FCSTD DOCUMENT  (FreeCAD 0.20R)
Label: id5
License: All rights reserved
LicenseURL: http://en.wikipedia.org/wiki/All_rights_reserved
objects: Part::Fillet×17, Part::FeaturePython×8, Sketcher::SketchObject×7, Part::Extrusion×7, Part::Chamfer×4, Drawing::FeatureViewPart×2, Drawing::FeaturePage×1, Part::MultiFuse×1, Part::Box×1, Part::Cut×1
note: 46 computed .brp shape members not serialized (recipe doc carries the construction recipe); baked Part::Feature solids carry a one-line shape summary decoded from their .brp

FEATURE [Sketcher::SketchObject] Sketch  label="Плата"
  FullyConstrained = false
  MapMode = 2
  Placement = pos=(91,0,0) rot=(0,0,1;0rad)
  sketch-geometry (16):
    g0: LineSegment StartX=-40.8321 StartY=93.3922 StartZ=0 EndX=42.1679 EndY=93.3922 EndZ=0
    g1: LineSegment StartX=42.1679 StartY=93.3922 StartZ=0 EndX=42.1679 EndY=15.3922 EndZ=0
    g2: LineSegment StartX=42.1679 StartY=15.3922 StartZ=0 EndX=-40.8321 EndY=15.3922 EndZ=0
    g3: LineSegment StartX=-40.8321 StartY=15.3922 StartZ=0 EndX=-40.8321 EndY=93.3922 EndZ=0
    g4: Circle CenterX=-38.5461 CenterY=91.1067 CenterZ=0 NormalX=0 NormalY=0 NormalZ=1 AngleXU=0 Radius=1.524
    g5: Circle CenterX=39.6579 CenterY=91.1022 CenterZ=0 NormalX=0 NormalY=0 NormalZ=1 AngleXU=0 Radius=1.524
    g6: LineSegment StartX=-38.5461 StartY=91.1067 StartZ=0 EndX=-40.8321 EndY=91.1067 EndZ=0
    g7: LineSegment StartX=-38.5461 StartY=91.1067 StartZ=0 EndX=-38.4965 EndY=93.3922 EndZ=0
    g8: LineSegment StartX=39.6579 StartY=91.1022 StartZ=0 EndX=42.1679 EndY=91.1022 EndZ=0
    g9: LineSegment StartX=39.6579 StartY=91.1022 StartZ=0 EndX=39.6579 EndY=93.3922 EndZ=0
    g10: Circle CenterX=-38.5461 CenterY=17.6782 CenterZ=0 NormalX=0 NormalY=0 NormalZ=1 AngleXU=0 Radius=1.524
    g11: LineSegment StartX=-38.5461 StartY=17.6782 StartZ=0 EndX=-40.8321 EndY=17.6782 EndZ=0
    g12: LineSegment StartX=-38.5461 StartY=17.6782 StartZ=0 EndX=-38.5461 EndY=15.3922 EndZ=0
    g13: Circle CenterX=39.7079 CenterY=17.7672 CenterZ=0 NormalX=0 NormalY=0 NormalZ=1 AngleXU=0 Radius=1.524
    g14: LineSegment StartX=39.7079 StartY=17.7672 StartZ=0 EndX=42.1679 EndY=17.7672 EndZ=0
    g15: LineSegment StartX=39.7079 StartY=17.7672 StartZ=0 EndX=39.7079 EndY=15.3922 EndZ=0
  constraints (44):
    c: Coincident(g1,g2)
    c: Coincident(g2,g3)
    c: Coincident(g3,g0)
    c: Horizontal(g0)
    c: Horizontal(g2)
    c: Vertical(g1)
    c: Vertical(g3)
    c: Distance(g1) = 78
    c: Distance(g2) = 83
    c: Radius(g4) = 1.524
    c: Coincident(g6,g4)
    c: PointOnObject(g6,g3)
    c: Horizontal(g6)
    c: Distance(g6) = 2.286
    c: Coincident(g7,g4)
    c: PointOnObject(g7,g0)
    c: Distance(g7) = 2.286
    c: Coincident(g8,g5)
    c: PointOnObject(g8,g1)
    c: Horizontal(g8)
    c: Distance(g8) = 2.51
    c: Coincident(g9,g5)
    c: PointOnObject(g9,g0)
    c: Vertical(g9)
    c: Distance(g9) = 2.29
    c: Coincident(g0,g1)
    c: Coincident(g11,g10)
    c: PointOnObject(g11,g3)
    c: Horizontal(g11)
    c: Coincident(g12,g10)
    c: PointOnObject(g12,g2)
    c: Vertical(g12)
    c: Distance(g11) = 2.286
    c: Distance(g12) = 2.286
    c: Radius(g10) = 1.524
    c: Equal(g10,g5)
    c: Coincident(g14,g13)
    c: PointOnObject(g14,g1)
    c: Horizontal(g14)
    c: Coincident(g15,g13)
    c: PointOnObject(g15,g2)
    c: Vertical(g15)
    c: Distance(g14) = 2.46
    c: Distance(g15) = 2.375
FEATURE [Sketcher::SketchObject] Sketch001  label="Дно"
  ExternalGeometry = -> [Sketch]
  FullyConstrained = false
  sketch-geometry (10):
    g0: LineSegment StartX=50.1679 StartY=886.008 StartZ=0 EndX=40.1679 EndY=886.008 EndZ=0
    g1: Circle CenterX=52.4539 CenterY=91.1067 CenterZ=0 NormalX=0 NormalY=0 NormalZ=1 AngleXU=0 Radius=1.524
    g2: Circle CenterX=130.658 CenterY=91.1022 CenterZ=0 NormalX=0 NormalY=0 NormalZ=1 AngleXU=0 Radius=1.524
    g3: Circle CenterX=130.708 CenterY=17.7672 CenterZ=0 NormalX=0 NormalY=0 NormalZ=1 AngleXU=0 Radius=1.524
    g4: Circle CenterX=52.4539 CenterY=17.6782 CenterZ=0 NormalX=0 NormalY=0 NormalZ=1 AngleXU=0 Radius=1.524
    g5: LineSegment StartX=883.638 StartY=93.3922 StartZ=0 EndX=883.638 EndY=103.392 EndZ=0
    g6: LineSegment StartX=47.1679 StartY=96.3922 StartZ=0 EndX=136.168 EndY=96.3922 EndZ=0
    g7: LineSegment StartX=136.168 StartY=96.3922 StartZ=0 EndX=136.168 EndY=12.3922 EndZ=0
    g8: LineSegment StartX=136.168 StartY=12.3922 StartZ=0 EndX=47.1679 EndY=12.3922 EndZ=0
    g9: LineSegment StartX=47.1679 StartY=12.3922 StartZ=0 EndX=47.1679 EndY=96.3922 EndZ=0
  constraints (8):
    c: Coincident(g6,g7)
    c: Coincident(g7,g8)
    c: Coincident(g8,g9)
    c: Coincident(g9,g6)
    c: Horizontal(g6)
    c: Horizontal(g8)
    c: Vertical(g7)
    c: Vertical(g9)
FEATURE [Part::Extrusion] Extrude  label="Плата002"
  Base = -> Sketch
  Dir = (0,0,1)
  DirMode = 2
  FaceMakerClass = Part::FaceMakerBullseye
  LengthFwd = 1.58
  LengthRev = 0
  Placement = pos=(0,0,4) rot=(0,0,1;0rad)
  Solid = true
  Symmetric = false
FEATURE [Part::Extrusion] Extrude001  label="Дно002"
  Base = -> Sketch001
  Dir = (0,0,1)
  DirMode = 2
  FaceMakerClass = Part::FaceMakerBullseye
  LengthFwd = 1.5
  LengthRev = 0
  Reversed = true
  Solid = true
  Symmetric = false
FEATURE [Sketcher::SketchObject] Sketch002
  ExternalGeometry = -> [Sketch001]
  FullyConstrained = true
  Placement = pos=(0,0,0) rot=(0.57735,0.57735,0.57735;2.0944rad)
  sketch-geometry (4):
    g0: LineSegment StartX=96.3922 StartY=30 StartZ=0 EndX=12.3822 EndY=30 EndZ=0
    g1: LineSegment StartX=12.3822 StartY=30 StartZ=0 EndX=12.3822 EndY=0 EndZ=0
    g2: LineSegment StartX=12.3822 StartY=0 StartZ=0 EndX=96.3922 EndY=0 EndZ=0
    g3: LineSegment StartX=96.3922 StartY=0 StartZ=0 EndX=96.3922 EndY=30 EndZ=0
  constraints (11):
    c: Coincident(g0,g1)
    c: Horizontal(g0)
    c: Vertical(g1)
    c: Coincident(g2,g1)
    c: Coincident(g2,g-3)
    c: Horizontal(g2)
    c: Coincident(g3,g2)
    c: Coincident(g3,g0)
    c: Vertical(g3)
    c: Distance(g1) = 30
    c: Distance(g0) = 84.01
FEATURE [Part::Extrusion] Extrude002  label="Стенка левая"
  Base = -> Sketch002
  Dir = (1,0,0)
  DirMode = 2
  FaceMakerClass = Part::FaceMakerBullseye
  LengthFwd = 1.5
  LengthRev = 0
  Placement = pos=(47.1679,0.01,0) rot=(0,0,1;0rad)
  Solid = true
  Symmetric = false
FEATURE [Sketcher::SketchObject] Sketch003
  FullyConstrained = false
  Placement = pos=(0,0,0) rot=(0.57735,0.57735,0.57735;2.0944rad)
  expr: Constraints[8] = Sketch002.Constraints[9]
  expr: Constraints[9] = Sketch002.Constraints[10]
  sketch-geometry (4):
    g0: LineSegment StartX=96.3922 StartY=30 StartZ=0 EndX=12.3822 EndY=30 EndZ=0
    g1: LineSegment StartX=12.3822 StartY=30 StartZ=0 EndX=12.3822 EndY=0 EndZ=0
    g2: LineSegment StartX=12.3822 StartY=0 StartZ=0 EndX=96.3922 EndY=0 EndZ=0
    g3: LineSegment StartX=96.3922 StartY=0 StartZ=0 EndX=96.3922 EndY=30 EndZ=0
  constraints (10):
    c: Coincident(g0,g1)
    c: Horizontal(g0)
    c: Vertical(g1)
    c: Coincident(g2,g1)
    c: Horizontal(g2)
    c: Coincident(g3,g2)
    c: Coincident(g3,g0)
    c: Vertical(g3)
    c: Distance(g1) = 30
    c: Distance(g0) = 84.01
FEATURE [Sketcher::SketchObject] Sketch005
  FullyConstrained = false
  Placement = pos=(0,0,0) rot=(1,0,0;1.5708rad)
  sketch-geometry (14):
    g0: LineSegment StartX=54.1679 StartY=14.9181 StartZ=0 EndX=66.1679 EndY=14.9181 EndZ=0
    g1: LineSegment StartX=66.1679 StartY=14.9181 StartZ=0 EndX=66.1679 EndY=4.91813 EndZ=0
    g2: LineSegment StartX=54.1679 StartY=4.91813 StartZ=0 EndX=54.1679 EndY=14.9181 EndZ=0
    g3: LineSegment StartX=100.097 StartY=14.9153 StartZ=0 EndX=112.097 EndY=14.9153 EndZ=0
    g4: LineSegment StartX=112.097 StartY=14.9153 StartZ=0 EndX=112.097 EndY=4.91528 EndZ=0
    g5: LineSegment StartX=100.097 StartY=4.91528 StartZ=0 EndX=100.097 EndY=14.9153 EndZ=0
    g6: LineSegment StartX=48.6586 StartY=30.0019 StartZ=0 EndX=134.673 EndY=30.0018 EndZ=0
    g7: LineSegment StartX=134.673 StartY=-0.0864853 StartZ=0 EndX=48.6586 EndY=-0.0811942 EndZ=0
    g8: LineSegment StartX=48.6586 StartY=-0.0811942 StartZ=0 EndX=48.6586 EndY=30.0019 EndZ=0
    g9: LineSegment StartX=134.673 StartY=-0.0864853 StartZ=0 EndX=134.673 EndY=30.0018 EndZ=0
    g10: LineSegment StartX=112.097 StartY=4.91528 StartZ=0 EndX=100.097 EndY=4.91528 EndZ=0
    g11: LineSegment StartX=66.1679 StartY=4.91813 StartZ=0 EndX=54.1679 EndY=4.91813 EndZ=0
    g12: LineSegment StartX=59.5738 StartY=4.91813 StartZ=0 EndX=59.5738 EndY=-0.0818657 EndZ=0
    g13: LineSegment StartX=105.94 StartY=4.91528 StartZ=0 EndX=105.94 EndY=-0.0847178 EndZ=0
  constraints (33):
    c: Coincident(g0,g1)
    c: Coincident(g2,g0)
    c: Horizontal(g0)
    c: Vertical(g1)
    c: Vertical(g2)
    c: Distance(g0) = 12
    c: Distance(g2) = 10
    c: Coincident(g3,g4)
    c: Coincident(g5,g3)
    c: Horizontal(g3)
    c: Vertical(g4)
    c: Vertical(g5)
    c: Equal(g5,g1)
    c: Equal(g3,g0)
    c: Coincident(g8,g6)
    c: Vertical(g8)
    c: Coincident(g9,g7)
    c: Coincident(g9,g6)
    c: Coincident(g10,g4)
    c: Coincident(g10,g5)
    c: Horizontal(g10)
    c: Coincident(g11,g1)
    c: Coincident(g11,g2)
    c: Horizontal(g11)
    c: Coincident(g7,g8)
    c: PointOnObject(g12,g11)
    c: PointOnObject(g12,g7)
    c: Vertical(g12)
    c: Distance(g12) = 5
    c: PointOnObject(g13,g10)
    c: PointOnObject(g13,g7)
    c: Vertical(g13)
    c: Equal(g13,g12)
FEATURE [Sketcher::SketchObject] Sketch006
  ExternalGeometry = -> [Sketch005,Sketch001]
  FullyConstrained = false
  sketch-geometry (20):
    g0: Circle CenterX=52.4539 CenterY=91.1067 CenterZ=0 NormalX=0 NormalY=0 NormalZ=1 AngleXU=0 Radius=1.524
    g1: Circle CenterX=130.658 CenterY=91.1022 CenterZ=0 NormalX=0 NormalY=0 NormalZ=1 AngleXU=0 Radius=1.524
    g2: Circle CenterX=130.708 CenterY=17.7672 CenterZ=0 NormalX=0 NormalY=0 NormalZ=1 AngleXU=0 Radius=1.524
    g3: Circle CenterX=52.4539 CenterY=17.6782 CenterZ=0 NormalX=0 NormalY=0 NormalZ=1 AngleXU=0 Radius=1.524
    g4: LineSegment StartX=89.2174 StartY=31.6922 StartZ=0 EndX=94.2174 EndY=31.6922 EndZ=0
    g5: LineSegment StartX=94.2174 StartY=31.6922 StartZ=0 EndX=94.2174 EndY=24.6922 EndZ=0
    g6: LineSegment StartX=94.2174 StartY=24.6922 StartZ=0 EndX=89.2174 EndY=24.6922 EndZ=0
    g7: LineSegment StartX=89.2174 StartY=24.6922 StartZ=0 EndX=89.2174 EndY=31.6922 EndZ=0
    g8: GeomPoint X=175.176 Y=40.8922 Z=0
    g9: LineSegment StartX=47.1679 StartY=96.3922 StartZ=0 EndX=47.1679 EndY=12.3922 EndZ=0
    g10: LineSegment StartX=47.1679 StartY=12.3922 StartZ=0 EndX=136.168 EndY=12.3922 EndZ=0
    g11: LineSegment StartX=136.168 StartY=12.3922 StartZ=0 EndX=136.168 EndY=96.3922 EndZ=0
    g12: LineSegment StartX=136.168 StartY=96.3922 StartZ=0 EndX=47.1679 EndY=96.3922 EndZ=0
    g13: LineSegment StartX=59.6679 StartY=83.8922 StartZ=0 EndX=123.668 EndY=83.8922 EndZ=0
    g14: LineSegment StartX=123.668 StartY=83.8922 StartZ=0 EndX=123.668 EndY=42.8922 EndZ=0
    g15: LineSegment StartX=123.668 StartY=42.8922 StartZ=0 EndX=59.6679 EndY=42.8922 EndZ=0
    g16: LineSegment StartX=59.6679 StartY=42.8922 StartZ=0 EndX=59.6679 EndY=83.8922 EndZ=0
    g17: LineSegment StartX=47.1679 StartY=62.2854 StartZ=0 EndX=59.6679 EndY=62.2854 EndZ=0
    g18: LineSegment StartX=123.668 StartY=63.2488 StartZ=0 EndX=136.168 EndY=63.2488 EndZ=0
    g19: LineSegment StartX=88.7526 StartY=83.8922 StartZ=0 EndX=88.7526 EndY=96.3922 EndZ=0
  constraints (45):
    c: DistanceX(g0) = 52.4539
    c: DistanceY(g2) = 17.7672
    c: Radius(g0) = 1.524
    c: Equal(g0,g1)
    c: Equal(g3,g1)
    c: Equal(g2,g1)
    c: Coincident(g4,g5)
    c: Coincident(g5,g6)
    c: Coincident(g6,g7)
    c: Coincident(g7,g4)
    c: Horizontal(g4)
    c: Horizontal(g6)
    c: Vertical(g5)
    c: Vertical(g7)
    c: Distance(g4) = 5
    c: Distance(g7) = 7
    c: Coincident(g9,g-4)
    c: Coincident(g9,g-5)
    c: Coincident(g10,g9)
    c: Coincident(g10,g-5)
    c: Coincident(g11,g10)
    c: Coincident(g11,g-4)
    c: Coincident(g12,g11)
    c: Coincident(g12,g9)
    c: Coincident(g13,g14)
    c: Coincident(g14,g15)
    c: Coincident(g15,g16)
    c: Coincident(g16,g13)
    c: Horizontal(g13)
    c: Horizontal(g15)
    c: Vertical(g14)
    c: Vertical(g16)
    c: Distance(g16) = 41
    c: Distance(g13) = 64
    c: PointOnObject(g17,g9)
    c: PointOnObject(g17,g16)
    c: Horizontal(g17)
    c: PointOnObject(g18,g14)
    c: PointOnObject(g18,g11)
    c: Horizontal(g18)
    c: Equal(g18,g17)
    c: PointOnObject(g19,g13)
    c: PointOnObject(g19,g12)
    c: Vertical(g19)
    c: Equal(g19,g18)
FEATURE [Part::Extrusion] Extrude006  label="Крышка"
  Base = -> Sketch006
  Dir = (0,0,1)
  DirMode = 2
  FaceMakerClass = Part::FaceMakerBullseye
  LengthFwd = 3
  LengthRev = 0
  Placement = pos=(0,0,30) rot=(0,0,1;0rad)
  Solid = true
  Symmetric = false
FEATURE [Drawing::FeatureViewPart] Ortho  label="Ortho_0_0"
  Direction = (0,0,1)
  HiddenWidth = 0.15
  LineWidth = 0.35
  Rotation = 0
  ShowHiddenLines = false
  ShowSmoothLines = false
  Source = -> Extrude006
  Tolerance = 0.05
  ViewResult = <g id="Ortho_0_0"\n   transform="rotate(0,-10,140.392) translate(-10,140.392) scale(1,1)"\n  >\n<g   fill="none"\n   stroke="rgb(0, 0, 0)"\n   stroke-linecap="butt"\n   stroke-linejoin="miter"\n   stroke-width="0.350000"\n   transform="scale(1,-1)"\n  >\n<path id= "1" d=" M 47.1679 96.3922 L 47.1679 12.3922 " />\n<path id= "2" d=" M 47.1679 12.3922 L 136.168 12.3922 " />\n<path id= "3" d=" M 136.168 12.3922 L 136.168 96.3922 " />\n<path id= "4" d=" M 136.168 96.3922 L 47.1679 96.3922 " />\n<path id= "5" d=" M 59.6679 83.8922 L 123.668 83.8922 " />\n<path id= "6" d=" M 123.668 83.8922 L 123.668 42.8922 " />\n<path id= "7" d=" M 123.668 42.8922 L 59.6679 42.8922 " />\n<path id= "8" d=" M 59.6679 42.8922 L 59.6679 83.8922 " />\n<path id= "9" d=" M 89.2174 31.6922 L 94.2174 31.6922 " />\n<path id= "10" d=" M 94.2174 31.6922 L 94.2174 24.6922 " />\n<path id= "11" d=" M 94.2174 24.6922 L 89.2174 24.6922 " />\n<path id= "12" d=" M 89.2174 24.6922 L 89.2174 31.6922 " />\n<circle cx ="52.4539" cy ="17.6782" r ="1.524" /><circle cx ="130.708" cy ="17.7672" r ="1.524" /><circle cx ="130.658" cy ="91.1022" r ="1.524" /><circle cx ="52.4539" cy ="91.1067" r ="1.524" /></g>\n</g>
  Visible = false
  X = -10
  Y = 140.392
FEATURE [Drawing::FeatureViewPart] Ortho001  label="Ortho_0_001"
  Direction = (0,0,1)
  HiddenWidth = 0.15
  LineWidth = 0.35
  Rotation = 0
  ShowHiddenLines = false
  ShowSmoothLines = false
  Source = -> Extrude001
  Tolerance = 0.05
  ViewResult = <g id="Ortho_0_001"\n   transform="rotate(0,120,140.392) translate(120,140.392) scale(1,1)"\n  >\n<g   fill="none"\n   stroke="rgb(0, 0, 0)"\n   stroke-linecap="butt"\n   stroke-linejoin="miter"\n   stroke-width="0.350000"\n   transform="scale(1,-1)"\n  >\n<path id= "1" d=" M 47.1679 96.3922 L 136.168 96.3922 " />\n<path id= "2" d=" M 136.168 96.3922 L 136.168 12.3922 " />\n<path id= "3" d=" M 136.168 12.3922 L 47.1679 12.3922 " />\n<path id= "4" d=" M 47.1679 12.3922 L 47.1679 96.3922 " />\n<circle cx ="52.4539" cy ="17.6782" r ="1.524" /><circle cx ="130.708" cy ="17.7672" r ="1.524" /><circle cx ="130.658" cy ="91.1022" r ="1.524" /><circle cx ="52.4539" cy ="91.1067" r ="1.524" /></g>\n</g>
  Visible = false
  X = 120
  Y = 140.392
FEATURE [Drawing::FeaturePage] Page  label="Крышка и дно"
  EditableTexts = Verbkin M.S.\t | BOX ID5 | FreeCAD DRAWING | A4 | X / Y | 1 | 1 | 1 | 12.06.2023 | REV A
  Group = -> [Ortho,Ortho001]
  Template = <path>
FEATURE [Part::Extrusion] Extrude007  label="Стенка правая"
  Base = -> Sketch003
  Dir = (1,0,0)
  DirMode = 2
  FaceMakerClass = Part::FaceMakerBullseye
  LengthFwd = 1.5
  LengthRev = 0
  Placement = pos=(134.668,0.01,0) rot=(0,0,1;0rad)
  Solid = true
  Symmetric = false
FEATURE [Sketcher::SketchObject] Sketch004
  ExternalGeometry = -> [Extrude002,Extrude007]
  FullyConstrained = false
  MapMode = 3
  Placement = pos=(0,0,0) rot=(1,0,0;1.5708rad)
  Support = -> [Sketch001]
  sketch-geometry (4):
    g0: LineSegment StartX=48.6586 StartY=30.0019 StartZ=0 EndX=134.673 EndY=30.0018 EndZ=0
    g1: LineSegment StartX=134.673 StartY=-0.003143 StartZ=0 EndX=48.6586 EndY=-0.006059 EndZ=0
    g2: LineSegment StartX=48.6586 StartY=30.0019 StartZ=0 EndX=48.6586 EndY=-0.006059 EndZ=0
    g3: LineSegment StartX=134.673 StartY=30.0018 StartZ=0 EndX=134.673 EndY=-0.003143 EndZ=0
  constraints (6):
    c: Coincident(g2,g0)
    c: Coincident(g2,g1)
    c: Vertical(g2)
    c: Coincident(g3,g0)
    c: Coincident(g3,g1)
    c: Vertical(g3)
FEATURE [Part::Extrusion] Extrude004  label="Стенка нижняя"
  Base = -> Sketch004
  Dir = (0,-1,2e-16)
  DirMode = 2
  FaceMakerClass = Part::FaceMakerBullseye
  LengthFwd = 3
  LengthRev = 0
  Placement = pos=(0.00930858,15.3922,0.006059) rot=(0,0,1;0rad)
  Solid = true
  Symmetric = false
FEATURE [Part::Extrusion] Extrude008  label="Стенка верхняя"
  Base = -> Sketch005
  Dir = (0,-1,1.1e-15)
  DirMode = 2
  FaceMakerClass = Part::FaceMakerBullseye
  LengthFwd = 1.5
  LengthRev = 0
  Placement = pos=(0.00930858,96.4022,0.006059) rot=(0,0,1;0rad)
  Solid = true
  Symmetric = false
FEATURE [Part::Fillet] Fillet
  Base = -> Extrude001
  Edges = 1 edges r=1: [Edge1]
FEATURE [Part::Fillet] Fillet001
  Base = -> Extrude002
  Edges = 1 edges r=1: [Edge11]
FEATURE [Part::Fillet] Fillet002
  Base = -> Fillet
  Edges = 1 edges r=1: [Edge23]
FEATURE [Part::Fillet] Fillet003
  Base = -> Fillet001
  Edges = 1 edges r=1: [Edge13]
FEATURE [Part::Fillet] Fillet004
  Base = -> Fillet002
  Edges = 1 edges r=1: [Edge19]
FEATURE [Part::Fillet] Fillet005
  Base = -> Extrude007
  Edges = 1 edges r=1: [Edge7]
FEATURE [Part::Fillet] Fillet006
  Base = -> Fillet004
  Edges = 1 edges r=1: [Edge20]
FEATURE [Part::Fillet] Fillet008
  Base = -> Extrude006
  Edges = 1 edges r=1: [Edge2]
FEATURE [Part::FeaturePython] Screw  label="M2.5x40-Винт"  # Fasteners workbench fastener (typed FeaturePython)
  Placement = pos=(52.45,91,-2.09) rot=(0,1,0;3.14159rad)
  diameter = 3
  invert = false
  leftHanded = false
  length = 10
  lengthCustom = 40
  matchOuter = false
  offset = 0
  thread = true
  type = 47
FEATURE [Part::FeaturePython] Nut  label="M3-Гайка"  # Fasteners workbench fastener (typed FeaturePython)
  Placement = pos=(130.708,17.7672,33) rot=(0,0,1;0rad)
  diameter = 1
  invert = false
  leftHanded = false
  matchOuter = false
  offset = 0
  thread = false
  type = 21
FEATURE [Part::Fillet] Fillet009
  Base = -> Fillet008
  Edges = 1 edges r=1: [Edge43]
FEATURE [Part::Fillet] Fillet010  label="Крышка001"
  Base = -> Fillet009
  Edges = 2 edges r=1: [Edge29,Edge30]
FEATURE [Part::MultiFuse] Fusion
  Shapes = -> [Extrude004,Extrude008,Fillet003,Fillet005,Fillet006]
FEATURE [Part::Fillet] Fillet011
  Base = -> Fusion
  Edges = 1 edges r=1: [Edge58]
FEATURE [Part::Chamfer] Chamfer
  Base = -> Fillet011
  Edges = 1 edges r=1: [Edge118]
FEATURE [Part::Chamfer] Chamfer001
  Base = -> Chamfer
  Edges = 1 edges r=1: [Edge10]
FEATURE [Part::Chamfer] Chamfer002
  Base = -> Chamfer001
  Edges = 1 edges r=1: [Edge11]
FEATURE [Part::Chamfer] Chamfer003  label="корпус"
  Base = -> Chamfer002
  Edges = 1 edges r=1: [Edge12]
FEATURE [Part::Fillet] Fillet012
  Base = -> Fillet010
  Edges = 1 edges r=1: [Edge54]
FEATURE [Part::Fillet] Fillet013  label="Крышка002"
  Base = -> Fillet012
  Edges = 3 edges r=1: [Edge4,Edge33,Edge34]
FEATURE [Part::FeaturePython] Screw001  label="M2.5x40-Винт001"  # Fasteners workbench fastener (typed FeaturePython)
  Placement = pos=(52.45,17.68,-2.09) rot=(0,1,0;3.14159rad)
  diameter = 3
  invert = false
  leftHanded = false
  length = 10
  lengthCustom = 40
  matchOuter = false
  offset = 0
  thread = true
  type = 47
FEATURE [Part::FeaturePython] Screw002  label="M2.5x40-Винт002"  # Fasteners workbench fastener (typed FeaturePython)
  Placement = pos=(130.66,91.1,-2.04) rot=(0,1,0;3.14159rad)
  diameter = 3
  invert = false
  leftHanded = false
  length = 10
  lengthCustom = 40
  matchOuter = false
  offset = 0
  thread = true
  type = 47
FEATURE [Part::FeaturePython] Screw003  label="M2.5x40-Винт003"  # Fasteners workbench fastener (typed FeaturePython)
  Placement = pos=(130.71,17.77,-2.04) rot=(0,1,0;3.14159rad)
  diameter = 3
  invert = false
  leftHanded = false
  length = 10
  lengthCustom = 40
  matchOuter = false
  offset = 0
  thread = true
  type = 47
FEATURE [Part::FeaturePython] Nut001  label="M3-Гайка001"  # Fasteners workbench fastener (typed FeaturePython)
  Placement = pos=(52.4539,91.1067,33) rot=(0,0,1;0rad)
  diameter = 1
  invert = false
  leftHanded = false
  matchOuter = false
  offset = 0
  thread = false
  type = 21
FEATURE [Part::FeaturePython] Nut002  label="M3-Гайка002"  # Fasteners workbench fastener (typed FeaturePython)
  Placement = pos=(52.4539,17.6782,33) rot=(0,0,1;0rad)
  diameter = 1
  invert = false
  leftHanded = false
  matchOuter = false
  offset = 0
  thread = false
  type = 21
FEATURE [Part::FeaturePython] Nut003  label="M3-Гайка003"  # Fasteners workbench fastener (typed FeaturePython)
  Placement = pos=(130.658,91.1022,33) rot=(0,0,1;0rad)
  diameter = 1
  invert = false
  leftHanded = false
  matchOuter = false
  offset = 0
  thread = false
  type = 21
FEATURE [Part::Fillet] Fillet014
  Base = -> Fillet013
  Edges = 1 edges r=1: [Edge49]
FEATURE [Part::Fillet] Fillet015  label="крышка"
  Base = -> Fillet014
  Edges = 4 edges r=1: [Edge13,Edge14,Edge15,Edge16]
FEATURE [Part::Box] Box  label="Куб"
  AttacherType = Attacher::AttachEngine3D
  Height = 11
  Length = 20
  Placement = pos=(134,92,18) rot=(0,0,1;0rad)
  Width = 2.5
FEATURE [Part::Cut] Cut  label="корпус001"
  Base = -> Chamfer003
  Tool = -> Box
FEATURE [Part::Fillet] Fillet016
  Base = -> Cut
  Edges = 4 edges r=1: [Edge139,Edge140,Edge141,Edge142]
FEATURE [Part::Fillet] Fillet017
  Base = -> Fillet016
  Edges = 4 edges r=1: [Edge13,Edge14,Edge15,Edge16]
note: 1 file-system path scrubbed to <path> (originals preserved in the JSON sidecar)
